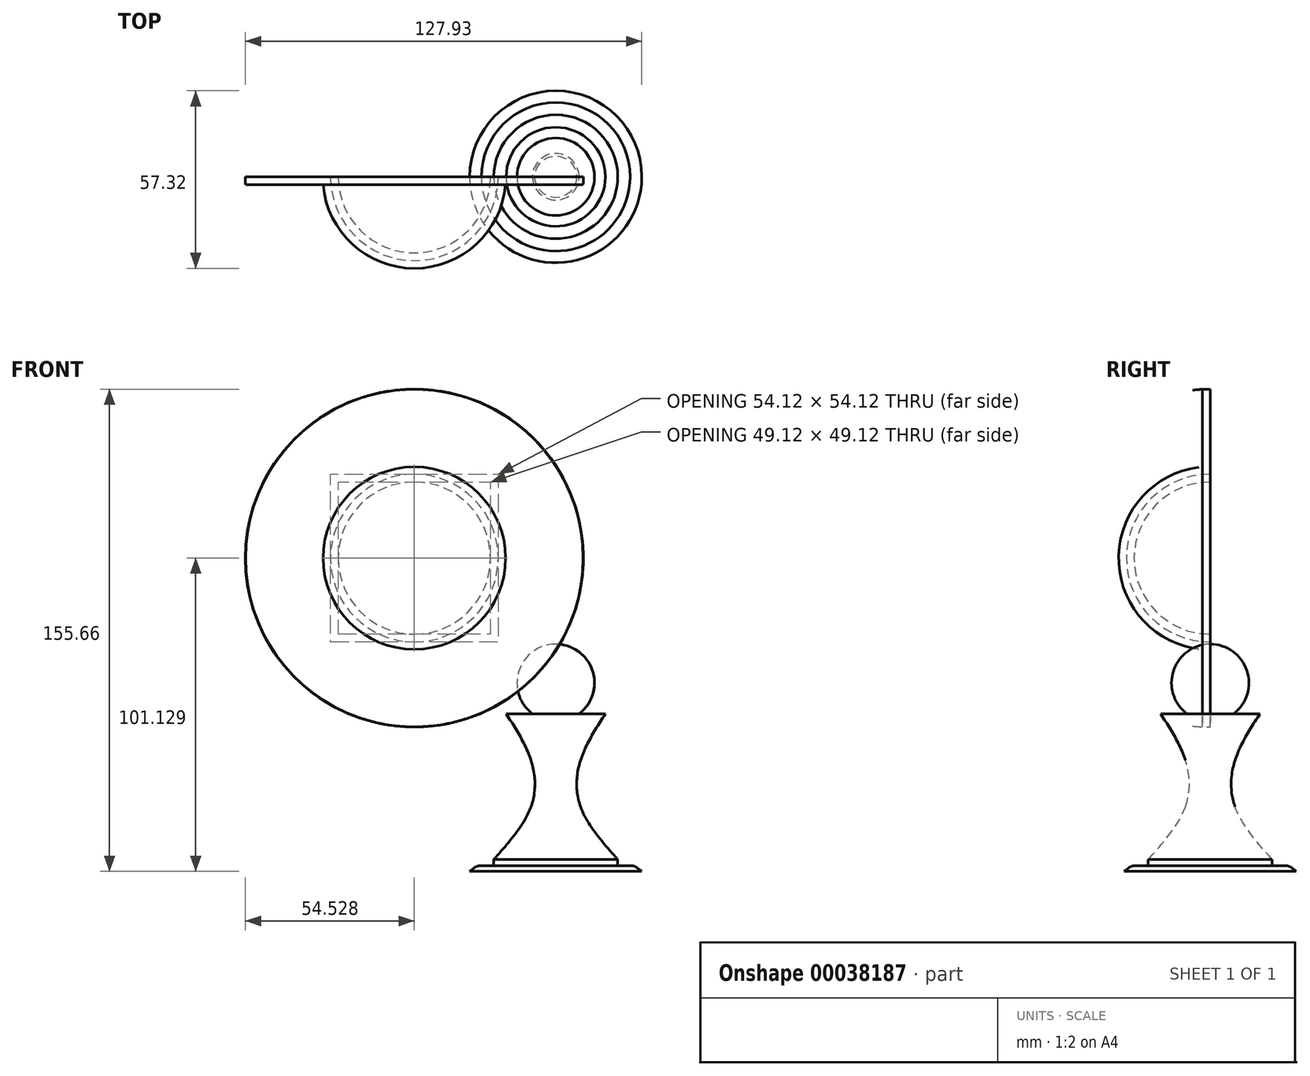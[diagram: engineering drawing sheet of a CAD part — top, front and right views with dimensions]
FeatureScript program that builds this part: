
annotation { "Feature Type Name" : "Feature", "Feature Type Description" : "" }
export const myFeature = defineFeature(function(context is Context, id is Id, definition is map)
    precondition{}
    {
        {
            var Q0;
            Q0=qCreatedBy(makeId("Front.planeOp"),FACE);
            var sketch = newSketch(context, id + "F0", { "sketchPlane" : qUnion([Q0])});
            skArc(sketch, "E0", {"start": v(7.5, -8.83) * mm, "mid": v(11.86, 5.12) * mm, "end": v(0, 13.67) * mm});
            skLineSegment(sketch, "E1", {"start": v(0, 1.17) * mm, "end": v(0, -8.83) * mm});
            skLineSegment(sketch, "E2", {"start": v(7.5, -8.83) * mm, "end": v(16, -8.83) * mm});
            skLineSegment(sketch, "E3", {"start": v(0, -8.83) * mm, "end": v(0, -23.83) * mm});
            skLineSegment(sketch, "E4", {"start": v(8, -23.83) * mm, "end": v(8, -38.83) * mm});
            skLineSegment(sketch, "E5", {"start": v(0, -38.83) * mm, "end": v(0, -53.83) * mm});
            skLineSegment(sketch, "E6", {"start": v(0, -53.83) * mm, "end": v(0, -55.83) * mm});
            skLineSegment(sketch, "E7", {"start": v(0, -55.83) * mm, "end": v(0, -57.83) * mm});
            skLineSegment(sketch, "E8", {"start": v(20, -57.83) * mm, "end": v(24, -57.83) * mm});
            skLineSegment(sketch, "E9", {"start": v(0, -57.83) * mm, "end": v(0, -59.7) * mm});
            skLineSegment(sketch, "E10", {"start": v(0, -59.7) * mm, "end": v(27.76, -59.7) * mm});
            skFitSpline(sketch, "E11", {"points": [v(16, -8.83) * mm, v(8, -23.83) * mm, v(8, -38.83) * mm, v(20, -55.83) * mm], "startDerivative": vector(-28.95, -44.76) * mm, "endDerivative": vector(40.8, -46.07) * mm});
            skFitSpline(sketch, "E12.trimOffspring", {"points": [v(16, -8.83) * mm, v(8, -23.83) * mm, v(8, -38.83) * mm, v(20, -55.83) * mm], "startDerivative": vector(-28.95, -44.76) * mm, "endDerivative": vector(40.8, -46.07) * mm});
            skLineSegment(sketch, "E13", {"start": v(0, -23.83) * mm, "end": v(0, -38.83) * mm});
            skLineSegment(sketch, "E14", {"start": v(20, -55.83) * mm, "end": v(20, -57.83) * mm});
            skFitSpline(sketch, "E15", {"points": [v(24, -57.83) * mm, v(25.46, -58.07) * mm, v(27.76, -59.7) * mm], "startDerivative": vector(3.38, -0.08) * mm, "endDerivative": vector(4.1, -3.48) * mm});
            skLineSegment(sketch, "E16", {"start": v(0, 13.67) * mm, "end": v(0, -11.33) * mm});
            skLineSegment(sketch, "E17", {"start": v(0, 13.67) * mm, "end": v(0, -59.7) * mm});
            skSolve(sketch);
        }
        {
            var Q0;
            {var subQ1=sQuery(id+"F0.wireOp",EDGE,"f2002512-f849-45ba-a12a-7bc720bd26c9");Q0=makeQuery(id+"F0.imprint","IMPRINT",FACE,{"disambiguationData":[TD([[makeQuery(id+"F0.imprint","IMPRINT",EDGE,{"derivedFrom":subQ1}),1.0]])]});}
            var Q1;
            {var subQ0=sQuery(id+"F0.wireOp",EDGE,"E17");var subQ3=sQuery(id+"F0.wireOp",EDGE,"E0");var subQ4=makeQuery(id+"F0.imprint","INTERSECT",VERTEX,{"disambiguationData":[OD(1.0)],"derivedFrom":[subQ3,subQ0]});Q1=makeQuery(id+"F0.imprint","IMPRINT",FACE,{"disambiguationData":[TD([[makeQuery(id+"F0.imprint","IMPRINT",EDGE,{"disambiguationData":[TD([[subQ4,1.0]])],"derivedFrom":subQ3}),1.0]])]});}
            var Q2;
            {var subQ0=sQuery(id+"F0.wireOp",EDGE,"E17");var subQ3=sQuery(id+"F0.wireOp",EDGE,"E0");var subQ4=makeQuery(id+"F0.imprint","INTERSECT",VERTEX,{"disambiguationData":[OD(0.0)],"derivedFrom":[subQ3,subQ0]});Q2=makeQuery(id+"F0.imprint","IMPRINT",FACE,{"disambiguationData":[TD([[makeQuery(id+"F0.imprint","IMPRINT",EDGE,{"disambiguationData":[TD([[subQ4,-1.0]])],"derivedFrom":subQ3}),1.0]])]});}
            var Q3;
            {var subQ2=sQuery(id+"F0.wireOp",EDGE,"f2002512-f849-45ba-a12a-7bc720bd26c9");Q3=makeQuery(id+"F0.imprint","IMPRINT",FACE,{"disambiguationData":[TD([[makeQuery(id+"F0.imprint","IMPRINT",EDGE,{"derivedFrom":subQ2}),-1.0]])]});}
            var Q4;
            {var subQ2=sQuery(id+"F0.wireOp",EDGE,"12ce5ff7-bd12-4778-b30c-90d4897b90e3");Q4=makeQuery(id+"F0.imprint","IMPRINT",FACE,{"disambiguationData":[TD([[makeQuery(id+"F0.imprint","IMPRINT",EDGE,{"derivedFrom":subQ2}),1.0]])]});}
            var Q5;
            {var subQ4=sQuery(id+"F0.wireOp",EDGE,"27071d47-daae-4ddc-a756-6a2a328ef6f9");Q5=makeQuery(id+"F0.imprint","IMPRINT",FACE,{"disambiguationData":[TD([[makeQuery(id+"F0.imprint","IMPRINT",EDGE,{"derivedFrom":subQ4}),-1.0]])]});}
            var Q6;
            {var subQ1=sQuery(id+"F0.wireOp",EDGE,"E10");Q6=makeQuery(id+"F0.imprint","IMPRINT",FACE,{"disambiguationData":[TD([[makeQuery(id+"F0.imprint","IMPRINT",EDGE,{"derivedFrom":subQ1}),1.0]])]});}
            var Q7;
            Q7=sQuery(id+"F0.wireOp",EDGE,"E17");
            revolve(context, id + "F1", {"entities" : qUnion([Q0, Q1, Q2, Q3, Q4, Q5, Q6]), "axis" : qUnion([Q7]), "revolveType" : RevolveType.FULL});
        }
        {
            var Q0;
            Q0=qCreatedBy(makeId("Front.planeOp"),FACE);
            var sketch = newSketch(context, id + "F2", { "sketchPlane" : qUnion([Q0])});
            skArc(sketch, "E18", {"start": v(-45.64, 14.37) * mm, "mid": v(-18.58, 41.43) * mm, "end": v(-45.64, 68.49) * mm});
            skLineSegment(sketch, "E19", {"start": v(-45.64, 68.49) * mm, "end": v(-45.64, 14.37) * mm});
            skCircle(sketch, "E20", {"center": v(-45.64, 41.43) * mm, "radius": 54.53 * mm});
            skLineSegment(sketch, "E21", {"start": v(-45.64, 95.96) * mm, "end": v(-45.64, -13.1) * mm});
            skSolve(sketch);
        }
        {
            var Q0;
            Q0=makeQuery(id+"F2.imprint","IMPRINT",FACE,{"disambiguationData":[TD([[makeQuery(id+"F2.imprint","IMPRINT",EDGE,{"derivedFrom":sQuery(id+"F2.wireOp",EDGE,"E18")}),1.0]])]});
            var Q1;
            Q1=sQuery(id+"F2.wireOp",EDGE,"E19");
            revolve(context, id + "F3", {"entities" : qUnion([Q0]), "axis" : qUnion([Q1]), "revolveType" : RevolveType.ONE_DIRECTION, "angle" : 180 * degree});
        }
        {
            var Q0;
            Q0=makeQuery(id+"F3.opRevolve","CAP_FACE",FACE,{"disambiguationData":[OSD([sQuery(id+"F2.wireOp",EDGE,"E18"),sQuery(id+"F2.wireOp",EDGE,"0a18ad6a-dcd1-4868-8c65-836a963b6b14")])],"isStart":true});
            shell(context, id + "F4", {"entities" : qUnion([Q0]), "thickness" : 2.5 * mm});
        }
        {
            var Q0;
            {var subQ3=sQuery(id+"F2.wireOp",EDGE,"E18");Q0=makeQuery(id+"F2.imprint","IMPRINT",FACE,{"disambiguationData":[TD([[makeQuery(id+"F2.imprint","IMPRINT",EDGE,{"derivedFrom":subQ3}),-1.0]])]});}
            var Q1;
            Q1=sQuery(id+"F2.wireOp",EDGE,"E21");
            revolve(context, id + "F5", {"entities" : qUnion([Q0]), "axis" : qUnion([Q1]), "revolveType" : RevolveType.ONE_DIRECTION, "angle" : 180 * degree});
        }
        {
            var Q0;
            Q0=makeQuery(id+"F5.opRevolve","SWEPT_FACE",FACE,{"disambiguationData":[OSD([sQuery(id+"F2.wireOp",EDGE,"E20")])]});
            shell(context, id + "F6", {"entities" : qUnion([Q0]), "thickness" : 2.5 * mm});
        }
    });
